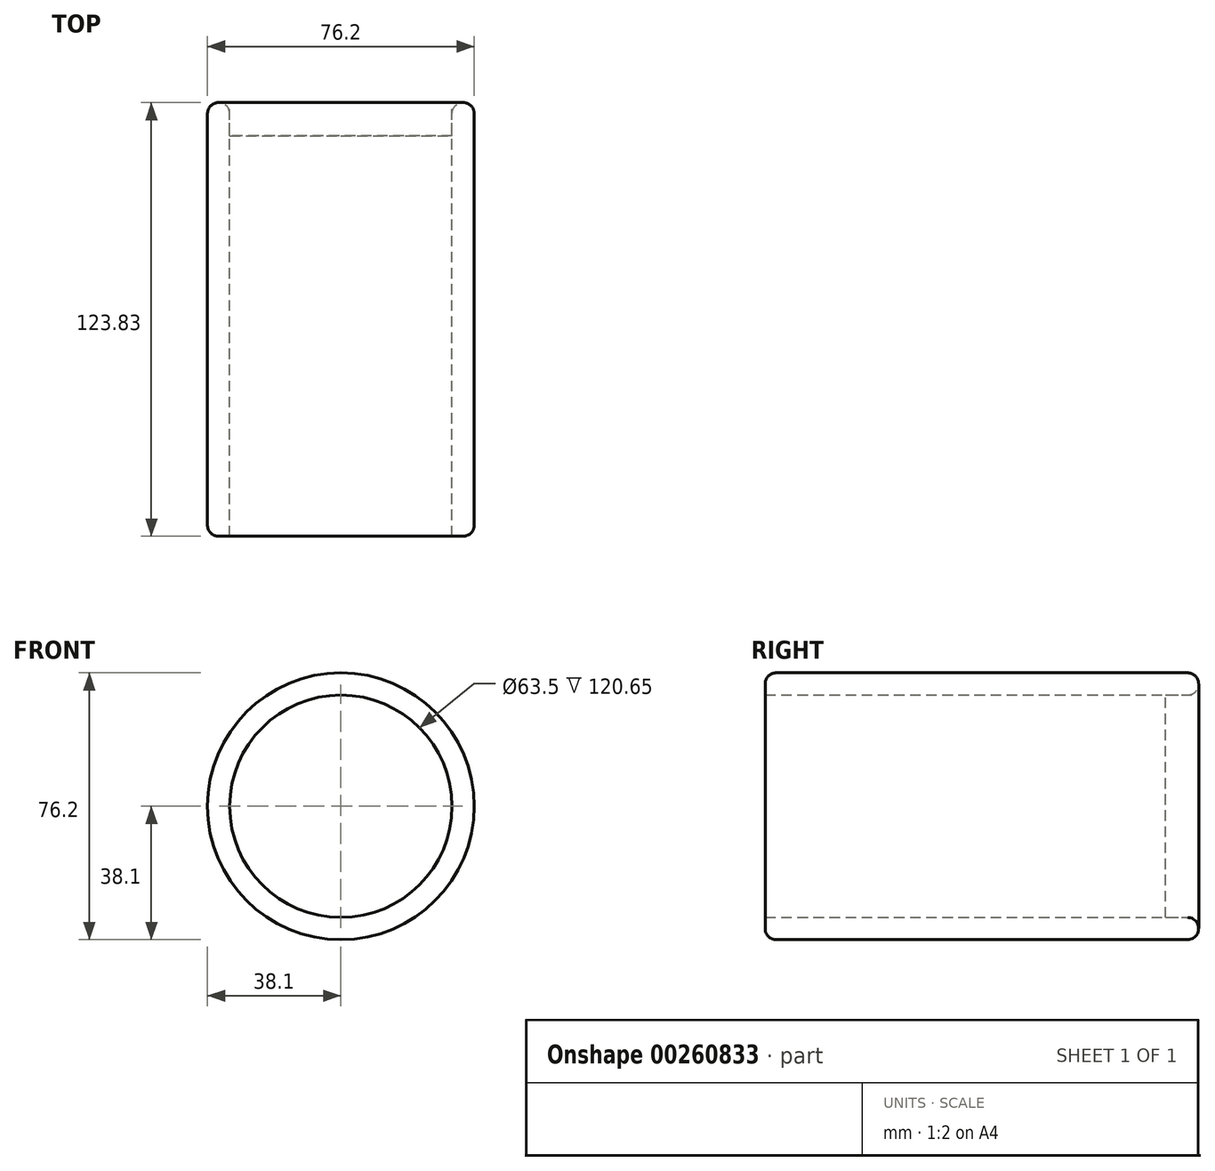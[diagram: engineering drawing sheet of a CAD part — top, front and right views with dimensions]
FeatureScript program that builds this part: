
annotation { "Feature Type Name" : "Feature", "Feature Type Description" : "" }
export const myFeature = defineFeature(function(context is Context, id is Id, definition is map)
    precondition{}
    {
        {
            var Q0;
            Q0=qCreatedBy(makeId("Front.planeOp"),FACE);
            var sketch = newSketch(context, id + "F0", { "sketchPlane" : qUnion([Q0])});
            skCircle(sketch, "E0", {"center": v(0, 0) * mm, "radius": 38.1 * mm});
            skCircle(sketch, "E1", {"center": v(0, 0) * mm, "radius": 31.75 * mm});
            skSolve(sketch);
        }
        {
            var Q0;
            Q0=makeQuery(id+"F0.imprint","IMPRINT",FACE,{"disambiguationData":[TD([[makeQuery(id+"F0.imprint","IMPRINT",EDGE,{"derivedFrom":sQuery(id+"F0.wireOp",EDGE,"E0")}),1.0]])]});
            extrude(context, id + "F1", {"entities" : qUnion([Q0]), "depth" : 123.82 * mm});
        }
        {
            var Q0;
            Q0=makeQuery(id+"F1.opExtrude","CAP_EDGE",EDGE,{"disambiguationData":[OSD([sQuery(id+"F0.wireOp",EDGE,"E0")])],"isStart":false});
            fillet(context, id + "F2", {"entities" : qUnion([Q0]), "radius" : 3.17 * mm, "tangentPropagation" : true, "allowEdgeOverflow" : false});
        }
        {
            var Q0;
            Q0=makeQuery(id+"F1.opExtrude","CAP_FACE",FACE,{"disambiguationData":[OSD([sQuery(id+"F0.wireOp",EDGE,"E0"),sQuery(id+"F0.wireOp",EDGE,"E1")])],"isStart":true});
            fillet(context, id + "F3", {"entities" : qUnion([Q0]), "radius" : 3.17 * mm, "tangentPropagation" : true, "allowEdgeOverflow" : false});
        }
        {
            var Q0;
            Q0=makeQuery(id+"F0.imprint","IMPRINT",FACE,{"disambiguationData":[TD([[makeQuery(id+"F0.imprint","IMPRINT",EDGE,{"derivedFrom":sQuery(id+"F0.wireOp",EDGE,"E1")}),1.0]])]});
            extrude(context, id + "F4", {"entities" : qUnion([Q0]), "depth" : 9.52 * mm});
        }
    });
